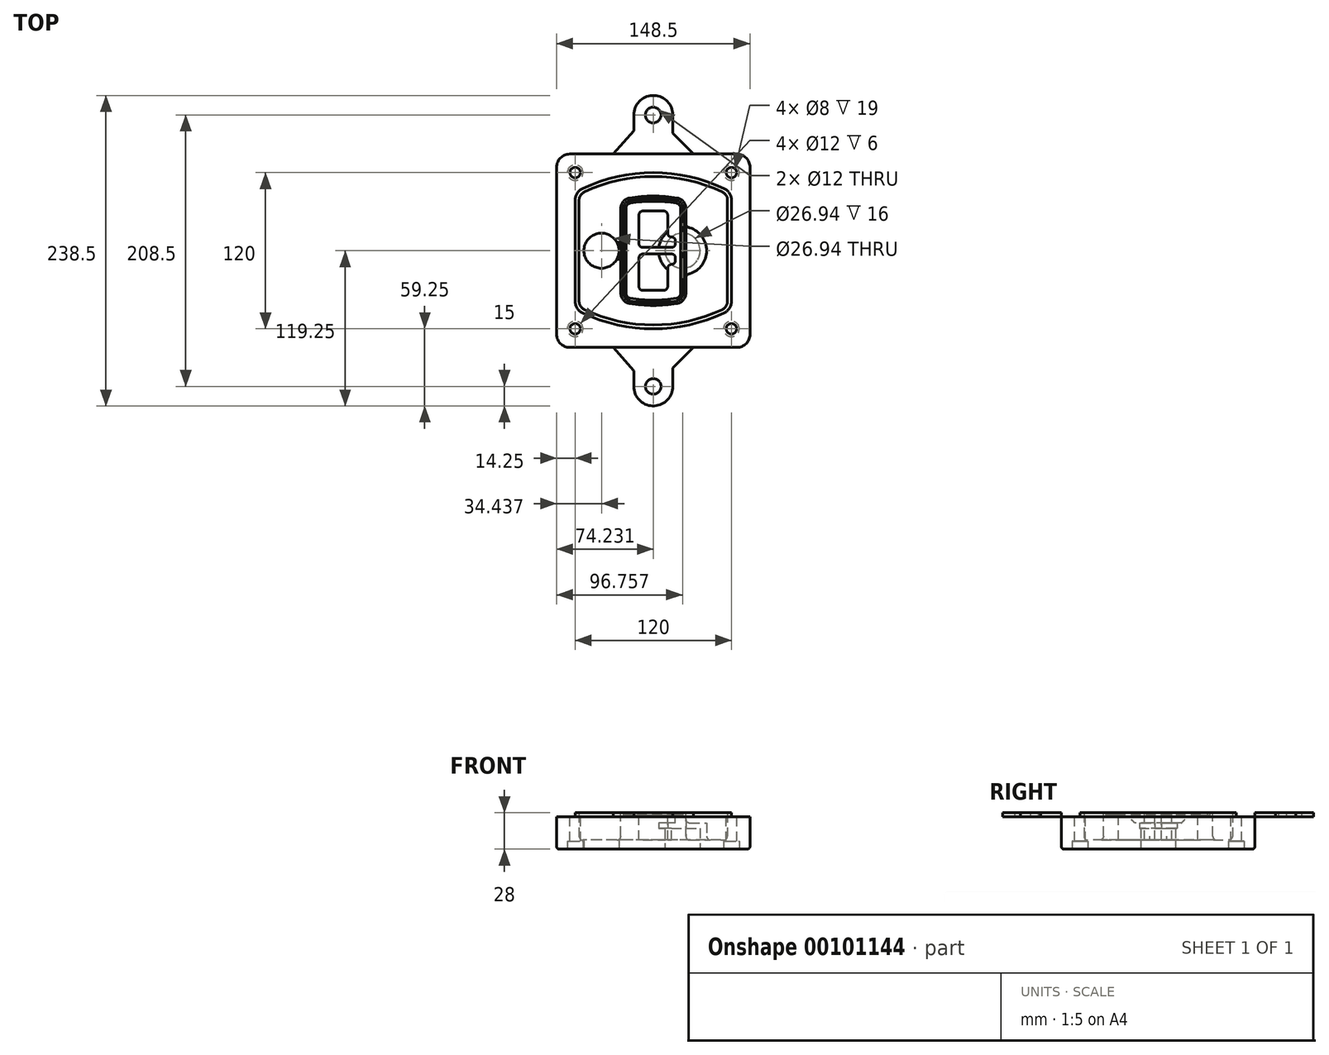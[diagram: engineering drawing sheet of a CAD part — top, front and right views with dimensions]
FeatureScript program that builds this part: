
annotation { "Feature Type Name" : "Feature", "Feature Type Description" : "" }
export const myFeature = defineFeature(function(context is Context, id is Id, definition is map)
    precondition{}
    {
        {
            var Q0;
            Q0=qCreatedBy(makeId("Top.planeOp"),FACE);
            var sketch = newSketch(context, id + "F0", { "sketchPlane" : qUnion([Q0])});
            skPoint(sketch, "E0.rect.middle", {"position": v(0, 0) * mm});
            skLineSegment(sketch, "E1.bottom", {"start": v(-64.25, -74.25) * mm, "end": v(64.25, -74.25) * mm});
            skLineSegment(sketch, "E1.top", {"start": v(-64.25, 74.25) * mm, "end": v(64.25, 74.25) * mm});
            skLineSegment(sketch, "E1.left", {"start": v(-74.25, -64.25) * mm, "end": v(-74.25, 64.25) * mm});
            skLineSegment(sketch, "E1.right", {"start": v(74.25, -64.25) * mm, "end": v(74.25, 64.25) * mm});
            skLineSegment(sketch, "E2", {"start": v(-74.25, 74.25) * mm, "end": v(74.25, -74.25) * mm, "construction": true});
            skLineSegment(sketch, "E3", {"start": v(74.25, 74.25) * mm, "end": v(-74.25, -74.25) * mm, "construction": true});
            skCircle(sketch, "E4", {"center": v(-60, 60) * mm, "radius": 4 * mm});
            skCircle(sketch, "E5", {"center": v(60, 60) * mm, "radius": 4 * mm});
            skCircle(sketch, "E6", {"center": v(60, -60) * mm, "radius": 4 * mm});
            skCircle(sketch, "E7", {"center": v(-60, -60) * mm, "radius": 4 * mm});
            skLineSegment(sketch, "E8", {"start": v(-60, 60) * mm, "end": v(60, 60) * mm, "construction": true});
            skLineSegment(sketch, "E9", {"start": v(60, 60) * mm, "end": v(60, -60) * mm, "construction": true});
            skLineSegment(sketch, "E10", {"start": v(60, -60) * mm, "end": v(-60, -60) * mm, "construction": true});
            skLineSegment(sketch, "E11", {"start": v(-60, -60) * mm, "end": v(-60, 60) * mm, "construction": true});
            skLineSegment(sketch, "E12", {"start": v(-60, 38.83) * mm, "end": v(-60, -38.83) * mm});
            skLineSegment(sketch, "E13", {"start": v(60, 38.83) * mm, "end": v(60, -38.83) * mm});
            skArc(sketch, "E14", {"start": v(54.26, 47.88) * mm, "mid": v(0, 60) * mm, "end": v(-54.26, 47.88) * mm});
            skArc(sketch, "E15", {"start": v(-54.26, -47.88) * mm, "mid": v(0, -60) * mm, "end": v(54.26, -47.88) * mm});
            skLineSegment(sketch, "E16", {"start": v(-60, 0) * mm, "end": v(60, 0) * mm, "construction": true});
            skPoint(sketch, "E17.visualSharp", {"position": v(-60, -45) * mm});
            skArc(sketch, "E17.filletArc", {"start": v(-60, -38.83) * mm, "mid": v(-58.44, -44.2) * mm, "end": v(-54.26, -47.88) * mm});
            skPoint(sketch, "E18.visualSharp", {"position": v(-60, 45) * mm});
            skArc(sketch, "E18.filletArc", {"start": v(-54.26, 47.88) * mm, "mid": v(-58.44, 44.2) * mm, "end": v(-60, 38.83) * mm});
            skPoint(sketch, "E19.visualSharp", {"position": v(60, 45) * mm});
            skArc(sketch, "E19.filletArc", {"start": v(60, 38.83) * mm, "mid": v(58.44, 44.2) * mm, "end": v(54.26, 47.88) * mm});
            skPoint(sketch, "E20.visualSharp", {"position": v(60, -45) * mm});
            skArc(sketch, "E20.filletArc", {"start": v(54.26, -47.88) * mm, "mid": v(58.44, -44.2) * mm, "end": v(60, -38.83) * mm});
            skPoint(sketch, "E21.visualSharp", {"position": v(-74.25, 74.25) * mm});
            skArc(sketch, "E21.filletArc", {"start": v(-64.25, 74.25) * mm, "mid": v(-71.32, 71.32) * mm, "end": v(-74.25, 64.25) * mm});
            skPoint(sketch, "E22.visualSharp", {"position": v(74.25, 74.25) * mm});
            skArc(sketch, "E22.filletArc", {"start": v(74.25, 64.25) * mm, "mid": v(71.32, 71.32) * mm, "end": v(64.25, 74.25) * mm});
            skPoint(sketch, "E23.visualSharp", {"position": v(74.25, -74.25) * mm});
            skArc(sketch, "E23.filletArc", {"start": v(64.25, -74.25) * mm, "mid": v(71.32, -71.32) * mm, "end": v(74.25, -64.25) * mm});
            skPoint(sketch, "E24.visualSharp", {"position": v(-74.25, -74.25) * mm});
            skArc(sketch, "E24.filletArc", {"start": v(-74.25, -64.25) * mm, "mid": v(-71.32, -71.32) * mm, "end": v(-64.25, -74.25) * mm});
            skArc(sketch, "E25.0", {"start": v(57, 38.83) * mm, "mid": v(55.9, 42.58) * mm, "end": v(52.98, 45.17) * mm});
            skLineSegment(sketch, "E25.1", {"start": v(57, 38.83) * mm, "end": v(57, -38.83) * mm});
            skArc(sketch, "E25.2", {"start": v(52.98, -45.17) * mm, "mid": v(55.9, -42.58) * mm, "end": v(57, -38.83) * mm});
            skArc(sketch, "E25.3", {"start": v(-52.98, -45.17) * mm, "mid": v(0, -57) * mm, "end": v(52.98, -45.17) * mm});
            skArc(sketch, "E25.4", {"start": v(-57, -38.83) * mm, "mid": v(-55.9, -42.58) * mm, "end": v(-52.98, -45.17) * mm});
            skArc(sketch, "E25.5", {"start": v(52.98, 45.17) * mm, "mid": v(0, 57) * mm, "end": v(-52.98, 45.17) * mm});
            skLineSegment(sketch, "E25.6", {"start": v(-57, 38.83) * mm, "end": v(-57, -38.83) * mm});
            skArc(sketch, "E25.7", {"start": v(-52.98, 45.17) * mm, "mid": v(-55.9, 42.58) * mm, "end": v(-57, 38.83) * mm});
            skArc(sketch, "E26.0", {"start": v(-55.96, 51.5) * mm, "mid": v(-61.82, 46.33) * mm, "end": v(-64, 38.83) * mm});
            skArc(sketch, "E26.1", {"start": v(55.96, 51.5) * mm, "mid": v(0, 64) * mm, "end": v(-55.96, 51.5) * mm});
            skArc(sketch, "E26.2", {"start": v(64, 38.83) * mm, "mid": v(61.82, 46.33) * mm, "end": v(55.96, 51.5) * mm});
            skLineSegment(sketch, "E26.3", {"start": v(64, 38.83) * mm, "end": v(64, -38.83) * mm});
            skArc(sketch, "E26.4", {"start": v(55.96, -51.5) * mm, "mid": v(61.82, -46.33) * mm, "end": v(64, -38.83) * mm});
            skLineSegment(sketch, "E26.5", {"start": v(-64, 38.83) * mm, "end": v(-64, -38.83) * mm});
            skArc(sketch, "E26.6", {"start": v(-55.96, -51.5) * mm, "mid": v(0, -64) * mm, "end": v(55.96, -51.5) * mm});
            skArc(sketch, "E26.7", {"start": v(-64, -38.83) * mm, "mid": v(-61.82, -46.33) * mm, "end": v(-55.96, -51.5) * mm});
            skSolve(sketch);
        }
        {
            var Q0;
            Q0=makeQuery(id+"F0.imprint","IMPRINT",FACE,{"disambiguationData":[TD([[makeQuery(id+"F0.imprint","IMPRINT",EDGE,{"derivedFrom":sQuery(id+"F0.wireOp",EDGE,"E1.bottom")}),1.0]])]});
            var Q1;
            Q1=makeQuery(id+"F0.imprint","IMPRINT",FACE,{"disambiguationData":[TD([[makeQuery(id+"F0.imprint","IMPRINT",EDGE,{"derivedFrom":sQuery(id+"F0.wireOp",EDGE,"E12")}),1.0]])]});
            var Q2;
            Q2=makeQuery(id+"F0.imprint","IMPRINT",FACE,{"disambiguationData":[TD([[makeQuery(id+"F0.imprint","IMPRINT",EDGE,{"derivedFrom":sQuery(id+"F0.wireOp",EDGE,"E25.0")}),1.0]])]});
            var Q3;
            Q3=makeQuery(id+"F0.imprint","IMPRINT",FACE,{"disambiguationData":[TD([[makeQuery(id+"F0.imprint","IMPRINT",EDGE,{"derivedFrom":sQuery(id+"F0.wireOp",EDGE,"E12")}),-1.0]])]});
            extrude(context, id + "F1", {"entities" : qUnion([Q0, Q1, Q2, Q3]), "oppositeDirection" : true, "depth" : 25 * mm});
        }
        {
            var Q0;
            Q0=makeQuery(id+"F0.imprint","IMPRINT",FACE,{"disambiguationData":[TD([[makeQuery(id+"F0.imprint","IMPRINT",EDGE,{"derivedFrom":sQuery(id+"F0.wireOp",EDGE,"E12")}),1.0]])]});
            extrude(context, id + "F2", {"entities" : qUnion([Q0]), "operationType" : NewBodyOperationType.ADD, "depth" : 3 * mm});
        }
        {
            var Q0;
            Q0=makeQuery(id+"F0.imprint","IMPRINT",FACE,{"disambiguationData":[TD([[makeQuery(id+"F0.imprint","IMPRINT",EDGE,{"derivedFrom":sQuery(id+"F0.wireOp",EDGE,"E25.0")}),1.0]])]});
            extrude(context, id + "F3", {"entities" : qUnion([Q0]), "operationType" : NewBodyOperationType.REMOVE, "oppositeDirection" : true, "depth" : 18 * mm});
        }
        {
            var Q0;
            Q0=makeQuery(id+"F2.opExtrude","CAP_FACE",FACE,{"disambiguationData":[OSD([sQuery(id+"F0.wireOp",EDGE,"E12"),sQuery(id+"F0.wireOp",EDGE,"E13"),sQuery(id+"F0.wireOp",EDGE,"E14"),sQuery(id+"F0.wireOp",EDGE,"E15"),sQuery(id+"F0.wireOp",EDGE,"E17.filletArc"),sQuery(id+"F0.wireOp",EDGE,"E18.filletArc"),sQuery(id+"F0.wireOp",EDGE,"E19.filletArc"),sQuery(id+"F0.wireOp",EDGE,"E20.filletArc"),sQuery(id+"F0.wireOp",EDGE,"E25.0"),sQuery(id+"F0.wireOp",EDGE,"E25.1"),sQuery(id+"F0.wireOp",EDGE,"E25.2"),sQuery(id+"F0.wireOp",EDGE,"E25.3"),sQuery(id+"F0.wireOp",EDGE,"E25.4"),sQuery(id+"F0.wireOp",EDGE,"E25.5"),sQuery(id+"F0.wireOp",EDGE,"E25.6"),sQuery(id+"F0.wireOp",EDGE,"E25.7")])],"isStart":false});
            var sketch = newSketch(context, id + "F4", { "sketchPlane" : qUnion([Q0])});
            skArc(sketch, "E27.0", {"start": v(-18.34, -40.45) * mm, "mid": v(0, -42) * mm, "end": v(18.34, -40.45) * mm});
            skArc(sketch, "E28.0", {"start": v(18.34, 40.45) * mm, "mid": v(0, 42) * mm, "end": v(-18.34, 40.45) * mm});
            skLineSegment(sketch, "E29", {"start": v(-25, 32.57) * mm, "end": v(-25, -32.57) * mm});
            skLineSegment(sketch, "E30", {"start": v(25, 32.57) * mm, "end": v(25, -32.57) * mm});
            skLineSegment(sketch, "E31", {"start": v(-25, 39.1) * mm, "end": v(25, 39.1) * mm, "construction": true});
            skLineSegment(sketch, "E32", {"start": v(-25, -39.1) * mm, "end": v(25, -39.1) * mm, "construction": true});
            skPoint(sketch, "E33.visualSharp", {"position": v(-25, 39.1) * mm});
            skArc(sketch, "E33.filletArc", {"start": v(-18.34, 40.45) * mm, "mid": v(-23.11, 37.73) * mm, "end": v(-25, 32.57) * mm});
            skPoint(sketch, "E34.visualSharp", {"position": v(25, 39.1) * mm});
            skArc(sketch, "E34.filletArc", {"start": v(25, 32.57) * mm, "mid": v(23.11, 37.73) * mm, "end": v(18.34, 40.45) * mm});
            skPoint(sketch, "E35.visualSharp", {"position": v(25, -39.1) * mm});
            skArc(sketch, "E35.filletArc", {"start": v(18.34, -40.45) * mm, "mid": v(23.11, -37.73) * mm, "end": v(25, -32.57) * mm});
            skPoint(sketch, "E36.visualSharp", {"position": v(-25, -39.1) * mm});
            skArc(sketch, "E36.filletArc", {"start": v(-25, -32.57) * mm, "mid": v(-23.11, -37.73) * mm, "end": v(-18.34, -40.45) * mm});
            skArc(sketch, "E37.0", {"start": v(52.98, 45.17) * mm, "mid": v(0, 57) * mm, "end": v(-52.98, 45.17) * mm});
            skArc(sketch, "E37.1", {"start": v(-52.98, 45.17) * mm, "mid": v(-55.9, 42.58) * mm, "end": v(-57, 38.83) * mm});
            skLineSegment(sketch, "E37.2", {"start": v(-57, 38.83) * mm, "end": v(-57, -38.83) * mm});
            skArc(sketch, "E37.3", {"start": v(-57, -38.83) * mm, "mid": v(-55.9, -42.58) * mm, "end": v(-52.98, -45.17) * mm});
            skArc(sketch, "E37.4", {"start": v(-52.98, -45.17) * mm, "mid": v(0, -57) * mm, "end": v(52.98, -45.17) * mm});
            skArc(sketch, "E37.5", {"start": v(52.98, -45.17) * mm, "mid": v(55.9, -42.58) * mm, "end": v(57, -38.83) * mm});
            skLineSegment(sketch, "E37.6", {"start": v(57, 38.83) * mm, "end": v(57, -38.83) * mm});
            skArc(sketch, "E37.7", {"start": v(57, 38.83) * mm, "mid": v(55.9, 42.58) * mm, "end": v(52.98, 45.17) * mm});
            skLineSegment(sketch, "E38.0", {"start": v(23, 32.57) * mm, "end": v(23, -32.57) * mm});
            skArc(sketch, "E38.1", {"start": v(18, -38.48) * mm, "mid": v(21.58, -36.44) * mm, "end": v(23, -32.57) * mm});
            skArc(sketch, "E38.2", {"start": v(-18, -38.48) * mm, "mid": v(0, -40) * mm, "end": v(18, -38.48) * mm});
            skArc(sketch, "E38.3", {"start": v(-23, -32.57) * mm, "mid": v(-21.58, -36.44) * mm, "end": v(-18, -38.48) * mm});
            skLineSegment(sketch, "E38.4", {"start": v(-23, 32.57) * mm, "end": v(-23, -32.57) * mm});
            skArc(sketch, "E38.5", {"start": v(23, 32.57) * mm, "mid": v(21.58, 36.44) * mm, "end": v(18, 38.48) * mm});
            skArc(sketch, "E38.6", {"start": v(-18, 38.48) * mm, "mid": v(-21.58, 36.44) * mm, "end": v(-23, 32.57) * mm});
            skArc(sketch, "E38.7", {"start": v(18, 38.48) * mm, "mid": v(0, 40) * mm, "end": v(-18, 38.48) * mm});
            skArc(sketch, "E39.0", {"start": v(21, 32.57) * mm, "mid": v(20.06, 35.15) * mm, "end": v(17.67, 36.5) * mm});
            skLineSegment(sketch, "E39.1", {"start": v(21, 32.57) * mm, "end": v(21, -32.57) * mm});
            skArc(sketch, "E39.2", {"start": v(17.67, -36.5) * mm, "mid": v(20.06, -35.15) * mm, "end": v(21, -32.57) * mm});
            skArc(sketch, "E39.3", {"start": v(-17.67, -36.5) * mm, "mid": v(0, -38) * mm, "end": v(17.67, -36.5) * mm});
            skArc(sketch, "E39.4", {"start": v(-21, -32.57) * mm, "mid": v(-20.06, -35.15) * mm, "end": v(-17.67, -36.5) * mm});
            skArc(sketch, "E39.5", {"start": v(17.67, 36.5) * mm, "mid": v(0, 38) * mm, "end": v(-17.67, 36.5) * mm});
            skLineSegment(sketch, "E39.6", {"start": v(-21, 32.57) * mm, "end": v(-21, -32.57) * mm});
            skArc(sketch, "E39.7", {"start": v(-17.67, 36.5) * mm, "mid": v(-20.06, 35.15) * mm, "end": v(-21, 32.57) * mm});
            skLineSegment(sketch, "E40", {"start": v(-25, 0) * mm, "end": v(25, 0) * mm, "construction": true});
            skLineSegment(sketch, "E41", {"start": v(-11, 5.5) * mm, "end": v(-11, 27.5) * mm});
            skLineSegment(sketch, "E42", {"start": v(-8, 30.5) * mm, "end": v(8, 30.5) * mm});
            skLineSegment(sketch, "E43", {"start": v(11, 27.5) * mm, "end": v(11, 13.5) * mm});
            skLineSegment(sketch, "E44", {"start": v(14, 10.5) * mm, "end": v(14, 10.5) * mm});
            skLineSegment(sketch, "E45", {"start": v(17, 7.5) * mm, "end": v(17, 5.5) * mm});
            skLineSegment(sketch, "E46", {"start": v(14, 2.5) * mm, "end": v(-8, 2.5) * mm});
            skPoint(sketch, "E47.visualSharp", {"position": v(-11, 30.5) * mm});
            skArc(sketch, "E47.filletArc", {"start": v(-8, 30.5) * mm, "mid": v(-10.12, 29.62) * mm, "end": v(-11, 27.5) * mm});
            skPoint(sketch, "E48.visualSharp", {"position": v(11, 30.5) * mm});
            skArc(sketch, "E48.filletArc", {"start": v(11, 27.5) * mm, "mid": v(10.12, 29.62) * mm, "end": v(8, 30.5) * mm});
            skPoint(sketch, "E49.visualSharp", {"position": v(11, 10.5) * mm});
            skArc(sketch, "E49.filletArc", {"start": v(11, 13.5) * mm, "mid": v(11.88, 11.38) * mm, "end": v(14, 10.5) * mm});
            skPoint(sketch, "E50.visualSharp", {"position": v(17, 10.5) * mm});
            skArc(sketch, "E50.filletArc", {"start": v(17, 7.5) * mm, "mid": v(16.12, 9.62) * mm, "end": v(14, 10.5) * mm});
            skPoint(sketch, "E51.visualSharp", {"position": v(17, 2.5) * mm});
            skArc(sketch, "E51.filletArc", {"start": v(14, 2.5) * mm, "mid": v(16.12, 3.38) * mm, "end": v(17, 5.5) * mm});
            skPoint(sketch, "E52.visualSharp", {"position": v(-11, 2.5) * mm});
            skArc(sketch, "E52.filletArc", {"start": v(-11, 5.5) * mm, "mid": v(-10.12, 3.38) * mm, "end": v(-8, 2.5) * mm});
            skLineSegment(sketch, "E53.0.MirrorCS", {"start": v(14, -2.5) * mm, "end": v(-8, -2.5) * mm});
            skArc(sketch, "E54.0.MirrorCS", {"start": v(-11, -5.5) * mm, "mid": v(-10.12, -3.38) * mm, "end": v(-8, -2.5) * mm});
            skLineSegment(sketch, "E55.0.MirrorCS", {"start": v(-11, -5.5) * mm, "end": v(-11, -27.5) * mm});
            skArc(sketch, "E56.0.MirrorCS", {"start": v(-8, -30.5) * mm, "mid": v(-10.12, -29.62) * mm, "end": v(-11, -27.5) * mm});
            skLineSegment(sketch, "E57.0.MirrorCS", {"start": v(-8, -30.5) * mm, "end": v(8, -30.5) * mm});
            skArc(sketch, "E58.0.MirrorCS", {"start": v(11, -27.5) * mm, "mid": v(10.12, -29.62) * mm, "end": v(8, -30.5) * mm});
            skLineSegment(sketch, "E59.0.MirrorCS", {"start": v(11, -27.5) * mm, "end": v(11, -13.5) * mm});
            skArc(sketch, "E60.0.MirrorCS", {"start": v(11, -13.5) * mm, "mid": v(11.88, -11.38) * mm, "end": v(14, -10.5) * mm});
            skArc(sketch, "E61.0.MirrorCS", {"start": v(17, -7.5) * mm, "mid": v(16.12, -9.62) * mm, "end": v(14, -10.5) * mm});
            skLineSegment(sketch, "E62.0.MirrorCS", {"start": v(17, -7.5) * mm, "end": v(17, -5.5) * mm});
            skArc(sketch, "E63.0.MirrorCS", {"start": v(14, -2.5) * mm, "mid": v(16.12, -3.38) * mm, "end": v(17, -5.5) * mm});
            skSolve(sketch);
        }
        {
            var Q0;
            Q0=makeQuery(id+"F4.imprint","IMPRINT",FACE,{"disambiguationData":[TD([[makeQuery(id+"F4.imprint","IMPRINT",EDGE,{"derivedFrom":sQuery(id+"F4.wireOp",EDGE,"E27.0")}),1.0]])]});
            var Q1;
            Q1=makeQuery(id+"F4.imprint","IMPRINT",FACE,{"disambiguationData":[TD([[makeQuery(id+"F4.imprint","IMPRINT",EDGE,{"derivedFrom":sQuery(id+"F4.wireOp",EDGE,"E38.0")}),-1.0]])]});
            var Q2;
            Q2=makeQuery(id+"F4.imprint","IMPRINT",FACE,{"disambiguationData":[TD([[makeQuery(id+"F4.imprint","IMPRINT",EDGE,{"derivedFrom":sQuery(id+"F4.wireOp",EDGE,"E39.0")}),1.0]])]});
            extrude(context, id + "F5", {"entities" : qUnion([Q0, Q1, Q2]), "operationType" : NewBodyOperationType.ADD, "endBound" : BoundingType.UP_TO_NEXT, "oppositeDirection" : true, "depth" : 25 * mm});
        }
        {
            var Q0;
            Q0=makeQuery(id+"F4.imprint","IMPRINT",FACE,{"disambiguationData":[TD([[makeQuery(id+"F4.imprint","IMPRINT",EDGE,{"derivedFrom":sQuery(id+"F4.wireOp",EDGE,"E38.0")}),-1.0]])]});
            extrude(context, id + "F6", {"entities" : qUnion([Q0]), "operationType" : NewBodyOperationType.REMOVE, "oppositeDirection" : true, "depth" : 2 * mm});
        }
        {
            var Q0;
            Q0=makeQuery(id+"F1.opExtrude","CAP_FACE",FACE,{"disambiguationData":[OSD([sQuery(id+"F0.wireOp",EDGE,"E1.bottom"),sQuery(id+"F0.wireOp",EDGE,"E1.top"),sQuery(id+"F0.wireOp",EDGE,"E1.left"),sQuery(id+"F0.wireOp",EDGE,"E1.right"),sQuery(id+"F0.wireOp",EDGE,"E4"),sQuery(id+"F0.wireOp",EDGE,"E5"),sQuery(id+"F0.wireOp",EDGE,"E6"),sQuery(id+"F0.wireOp",EDGE,"E7"),sQuery(id+"F0.wireOp",EDGE,"E21.filletArc"),sQuery(id+"F0.wireOp",EDGE,"E22.filletArc"),sQuery(id+"F0.wireOp",EDGE,"E23.filletArc"),sQuery(id+"F0.wireOp",EDGE,"E24.filletArc")])],"isStart":false});
            var sketch = newSketch(context, id + "F7", { "sketchPlane" : qUnion([Q0])});
            skCircle(sketch, "E64", {"center": v(22.5, 0) * mm, "radius": 13.47 * mm});
            skCircle(sketch, "E65", {"center": v(-39.81, 0) * mm, "radius": 13.47 * mm});
            skLineSegment(sketch, "E66", {"start": v(74.25, 0) * mm, "end": v(-74.25, 0) * mm});
            skCircle(sketch, "E67", {"center": v(22.5, 0) * mm, "radius": 18.47 * mm});
            skCircle(sketch, "E68", {"center": v(60, -60) * mm, "radius": 6 * mm});
            skCircle(sketch, "E69", {"center": v(-60, -60) * mm, "radius": 6 * mm});
            skCircle(sketch, "E70", {"center": v(-60, 60) * mm, "radius": 6 * mm});
            skCircle(sketch, "E71", {"center": v(60, 60) * mm, "radius": 6 * mm});
            skSolve(sketch);
        }
        {
            var Q0;
            {var subQ1=sQuery(id+"F7.wireOp",EDGE,"E66");var subQ4=sQuery(id+"F7.wireOp",EDGE,"E64");var subQ6=makeQuery(id+"F7.imprint","INTERSECT",VERTEX,{"disambiguationData":[OD(0.0)],"derivedFrom":[subQ4,subQ1]});Q0=makeQuery(id+"F7.imprint","IMPRINT",FACE,{"disambiguationData":[TD([[makeQuery(id+"F7.imprint","IMPRINT",EDGE,{"disambiguationData":[TD([[subQ6,-1.0]])],"derivedFrom":subQ4}),-1.0]])]});}
            var Q1;
            {var subQ0=sQuery(id+"F7.wireOp",EDGE,"E66");var subQ1=sQuery(id+"F7.wireOp",EDGE,"E64");var subQ3=makeQuery(id+"F7.imprint","INTERSECT",VERTEX,{"disambiguationData":[OD(0.0)],"derivedFrom":[subQ1,subQ0]});Q1=makeQuery(id+"F7.imprint","IMPRINT",FACE,{"disambiguationData":[TD([[makeQuery(id+"F7.imprint","IMPRINT",EDGE,{"disambiguationData":[TD([[subQ3,-1.0]])],"derivedFrom":subQ1}),1.0]])]});}
            var Q2;
            {var subQ0=sQuery(id+"F7.wireOp",EDGE,"E66");var subQ1=sQuery(id+"F7.wireOp",EDGE,"E64");var subQ3=makeQuery(id+"F7.imprint","INTERSECT",VERTEX,{"disambiguationData":[OD(0.0)],"derivedFrom":[subQ1,subQ0]});Q2=makeQuery(id+"F7.imprint","IMPRINT",FACE,{"disambiguationData":[TD([[makeQuery(id+"F7.imprint","IMPRINT",EDGE,{"disambiguationData":[TD([[subQ3,1.0]])],"derivedFrom":subQ1}),1.0]])]});}
            var Q3;
            {var subQ1=sQuery(id+"F7.wireOp",EDGE,"E66");var subQ4=sQuery(id+"F7.wireOp",EDGE,"E64");var subQ6=makeQuery(id+"F7.imprint","INTERSECT",VERTEX,{"disambiguationData":[OD(0.0)],"derivedFrom":[subQ4,subQ1]});Q3=makeQuery(id+"F7.imprint","IMPRINT",FACE,{"disambiguationData":[TD([[makeQuery(id+"F7.imprint","IMPRINT",EDGE,{"disambiguationData":[TD([[subQ6,1.0]])],"derivedFrom":subQ4}),-1.0]])]});}
            extrude(context, id + "F8", {"entities" : qUnion([Q0, Q1, Q2, Q3]), "operationType" : NewBodyOperationType.ADD, "oppositeDirection" : true, "depth" : 20 * mm});
        }
        {
            var Q0;
            {var subQ0=sQuery(id+"F7.wireOp",EDGE,"E66");var subQ1=sQuery(id+"F7.wireOp",EDGE,"E64");var subQ3=makeQuery(id+"F7.imprint","INTERSECT",VERTEX,{"disambiguationData":[OD(0.0)],"derivedFrom":[subQ1,subQ0]});Q0=makeQuery(id+"F7.imprint","IMPRINT",FACE,{"disambiguationData":[TD([[makeQuery(id+"F7.imprint","IMPRINT",EDGE,{"disambiguationData":[TD([[subQ3,-1.0]])],"derivedFrom":subQ1}),1.0]])]});}
            var Q1;
            {var subQ0=sQuery(id+"F7.wireOp",EDGE,"E66");var subQ1=sQuery(id+"F7.wireOp",EDGE,"E64");var subQ3=makeQuery(id+"F7.imprint","INTERSECT",VERTEX,{"disambiguationData":[OD(0.0)],"derivedFrom":[subQ1,subQ0]});Q1=makeQuery(id+"F7.imprint","IMPRINT",FACE,{"disambiguationData":[TD([[makeQuery(id+"F7.imprint","IMPRINT",EDGE,{"disambiguationData":[TD([[subQ3,1.0]])],"derivedFrom":subQ1}),1.0]])]});}
            extrude(context, id + "F9", {"entities" : qUnion([Q0, Q1]), "operationType" : NewBodyOperationType.REMOVE, "oppositeDirection" : true, "depth" : 16 * mm});
        }
        {
            var Q0;
            {var subQ0=sQuery(id+"F7.wireOp",EDGE,"E66");var subQ1=sQuery(id+"F7.wireOp",EDGE,"E65");var subQ3=makeQuery(id+"F7.imprint","INTERSECT",VERTEX,{"disambiguationData":[OD(0.0)],"derivedFrom":[subQ1,subQ0]});Q0=makeQuery(id+"F7.imprint","IMPRINT",FACE,{"disambiguationData":[TD([[makeQuery(id+"F7.imprint","IMPRINT",EDGE,{"disambiguationData":[TD([[subQ3,-1.0]])],"derivedFrom":subQ1}),1.0]])]});}
            var Q1;
            {var subQ0=sQuery(id+"F7.wireOp",EDGE,"E66");var subQ1=sQuery(id+"F7.wireOp",EDGE,"E65");var subQ3=makeQuery(id+"F7.imprint","INTERSECT",VERTEX,{"disambiguationData":[OD(0.0)],"derivedFrom":[subQ1,subQ0]});Q1=makeQuery(id+"F7.imprint","IMPRINT",FACE,{"disambiguationData":[TD([[makeQuery(id+"F7.imprint","IMPRINT",EDGE,{"disambiguationData":[TD([[subQ3,1.0]])],"derivedFrom":subQ1}),1.0]])]});}
            extrude(context, id + "F10", {"entities" : qUnion([Q0, Q1]), "operationType" : NewBodyOperationType.REMOVE, "oppositeDirection" : true, "depth" : 25 * mm});
        }
        {
            var Q0;
            Q0=makeQuery(id+"F7.imprint","IMPRINT",FACE,{"disambiguationData":[TD([[makeQuery(id+"F7.imprint","IMPRINT",EDGE,{"derivedFrom":sQuery(id+"F7.wireOp",EDGE,"E68")}),1.0]])]});
            var Q1;
            Q1=makeQuery(id+"F7.imprint","IMPRINT",FACE,{"disambiguationData":[TD([[makeQuery(id+"F7.imprint","IMPRINT",EDGE,{"derivedFrom":makeQuery(id+"F1.opExtrude","CAP_EDGE",EDGE,{"disambiguationData":[OSD([sQuery(id+"F0.wireOp",EDGE,"E5")])],"isStart":false})}),-1.0]])]});
            var Q2;
            Q2=makeQuery(id+"F7.imprint","IMPRINT",FACE,{"disambiguationData":[TD([[makeQuery(id+"F7.imprint","IMPRINT",EDGE,{"derivedFrom":sQuery(id+"F7.wireOp",EDGE,"E69")}),1.0]])]});
            var Q3;
            Q3=makeQuery(id+"F7.imprint","IMPRINT",FACE,{"disambiguationData":[TD([[makeQuery(id+"F7.imprint","IMPRINT",EDGE,{"derivedFrom":makeQuery(id+"F1.opExtrude","CAP_EDGE",EDGE,{"disambiguationData":[OSD([sQuery(id+"F0.wireOp",EDGE,"E4")])],"isStart":false})}),-1.0]])]});
            var Q4;
            Q4=makeQuery(id+"F7.imprint","IMPRINT",FACE,{"disambiguationData":[TD([[makeQuery(id+"F7.imprint","IMPRINT",EDGE,{"derivedFrom":sQuery(id+"F7.wireOp",EDGE,"E70")}),1.0]])]});
            var Q5;
            Q5=makeQuery(id+"F7.imprint","IMPRINT",FACE,{"disambiguationData":[TD([[makeQuery(id+"F7.imprint","IMPRINT",EDGE,{"derivedFrom":makeQuery(id+"F1.opExtrude","CAP_EDGE",EDGE,{"disambiguationData":[OSD([sQuery(id+"F0.wireOp",EDGE,"E7")])],"isStart":false})}),-1.0]])]});
            var Q6;
            Q6=makeQuery(id+"F7.imprint","IMPRINT",FACE,{"disambiguationData":[TD([[makeQuery(id+"F7.imprint","IMPRINT",EDGE,{"derivedFrom":sQuery(id+"F7.wireOp",EDGE,"E71")}),1.0]])]});
            var Q7;
            Q7=makeQuery(id+"F7.imprint","IMPRINT",FACE,{"disambiguationData":[TD([[makeQuery(id+"F7.imprint","IMPRINT",EDGE,{"derivedFrom":makeQuery(id+"F1.opExtrude","CAP_EDGE",EDGE,{"disambiguationData":[OSD([sQuery(id+"F0.wireOp",EDGE,"E6")])],"isStart":false})}),-1.0]])]});
            extrude(context, id + "F11", {"entities" : qUnion([Q0, Q1, Q2, Q3, Q4, Q5, Q6, Q7]), "operationType" : NewBodyOperationType.REMOVE, "oppositeDirection" : true, "depth" : 6 * mm});
        }
        {
            var Q0;
            Q0=makeQuery(id+"F9.boolean.opBoolean","COPY",FACE,{"derivedFrom":makeQuery(id+"F9.opExtrude","CAP_FACE",FACE,{"disambiguationData":[OSD([sQuery(id+"F7.wireOp",EDGE,"E64")])],"isStart":false})});
            var sketch = newSketch(context, id + "F12", { "sketchPlane" : qUnion([Q0])});
            skArc(sketch, "E72.0", {"start": v(11, 14.45) * mm, "mid": v(6.45, 9.13) * mm, "end": v(4.2, 2.5) * mm});
            skArc(sketch, "E72.1", {"start": v(4.2, -2.5) * mm, "mid": v(6.45, -9.13) * mm, "end": v(11, -14.45) * mm});
            skLineSegment(sketch, "E73", {"start": v(4.2, -2.5) * mm, "end": v(14, -2.5) * mm});
            skLineSegment(sketch, "E74.0", {"start": v(14, 2.5) * mm, "end": v(4.2, 2.5) * mm});
            skArc(sketch, "E74.1", {"start": v(14, 2.5) * mm, "mid": v(16.12, 3.38) * mm, "end": v(17, 5.5) * mm});
            skLineSegment(sketch, "E74.2", {"start": v(17, 7.5) * mm, "end": v(17, 5.5) * mm});
            skArc(sketch, "E74.3", {"start": v(17, 7.5) * mm, "mid": v(16.12, 9.62) * mm, "end": v(14, 10.5) * mm});
            skArc(sketch, "E74.4", {"start": v(11, 13.5) * mm, "mid": v(11.88, 11.38) * mm, "end": v(14, 10.5) * mm});
            skLineSegment(sketch, "E74.5", {"start": v(11, 14.45) * mm, "end": v(11, 13.5) * mm});
            skLineSegment(sketch, "E74.7", {"start": v(14, -2.5) * mm, "end": v(4.2, -2.5) * mm});
            skArc(sketch, "E74.8", {"start": v(14, -2.5) * mm, "mid": v(16.12, -3.38) * mm, "end": v(17, -5.5) * mm});
            skLineSegment(sketch, "E74.9", {"start": v(17, -7.5) * mm, "end": v(17, -5.5) * mm});
            skArc(sketch, "E74.10", {"start": v(17, -7.5) * mm, "mid": v(16.12, -9.62) * mm, "end": v(14, -10.5) * mm});
            skArc(sketch, "E74.11", {"start": v(11, -13.5) * mm, "mid": v(11.88, -11.38) * mm, "end": v(14, -10.5) * mm});
            skLineSegment(sketch, "E74.12", {"start": v(11, -14.45) * mm, "end": v(11, -13.5) * mm});
            skPoint(sketch, "E75.orphan", {"position": v(11, -27.5) * mm});
            skPoint(sketch, "E76.orphan", {"position": v(-8, -2.5) * mm});
            skPoint(sketch, "E77.orphan", {"position": v(-8, 2.5) * mm});
            skPoint(sketch, "E78.orphan", {"position": v(11, 27.5) * mm});
            skSolve(sketch);
        }
        {
            var Q0;
            {var subQ7=sQuery(id+"F12.wireOp",EDGE,"E72.0");var subQ14=sQuery(id+"F12.wireOp",EDGE,"E72.1");var subQ16=sQuery(id+"F12.wireOp",EDGE,"E74.1");var subQ18=sQuery(id+"F12.wireOp",EDGE,"E74.8");Q0=qUnion([makeQuery(id+"F12.imprint","IMPRINT",FACE,{"disambiguationData":[TD([[makeQuery(id+"F12.imprint","IMPRINT",EDGE,{"derivedFrom":subQ7}),1.0]])]}),makeQuery(id+"F12.imprint","IMPRINT",FACE,{"disambiguationData":[TD([[makeQuery(id+"F12.imprint","IMPRINT",EDGE,{"derivedFrom":subQ14}),1.0]])]}),makeQuery(id+"F12.imprint","IMPRINT",FACE,{"disambiguationData":[TD([[makeQuery(id+"F12.imprint","IMPRINT",EDGE,{"derivedFrom":subQ16}),1.0]])]}),makeQuery(id+"F12.imprint","IMPRINT",FACE,{"disambiguationData":[TD([[makeQuery(id+"F12.imprint","IMPRINT",EDGE,{"derivedFrom":subQ18}),-1.0]])]})]);}
            var Q1;
            Q1=makeQuery(id+"F5.boolean.opBoolean","SPLIT",FACE,{"disambiguationData":[TD([makeQuery(id+"F5.opExtrude","SWEPT_FACE",FACE,{"disambiguationData":[OSD([sQuery(id+"F4.wireOp",EDGE,"E41")])]})])],"derivedFrom":makeQuery(id+"F3.boolean.opBoolean","COPY",FACE,{"derivedFrom":makeQuery(id+"F3.opExtrude","CAP_FACE",FACE,{"disambiguationData":[OSD([sQuery(id+"F0.wireOp",EDGE,"E25.0"),sQuery(id+"F0.wireOp",EDGE,"E25.1"),sQuery(id+"F0.wireOp",EDGE,"E25.2"),sQuery(id+"F0.wireOp",EDGE,"E25.3"),sQuery(id+"F0.wireOp",EDGE,"E25.4"),sQuery(id+"F0.wireOp",EDGE,"E25.5"),sQuery(id+"F0.wireOp",EDGE,"E25.6"),sQuery(id+"F0.wireOp",EDGE,"E25.7")])],"isStart":false})})});
            extrude(context, id + "F13", {"entities" : qUnion([Q0]), "operationType" : NewBodyOperationType.REMOVE, "endBound" : BoundingType.UP_TO_SURFACE, "endBoundEntityFace" : qUnion([Q1]), "depth" : 25 * mm});
        }
        {
            var Q0;
            Q0=makeQuery(id+"F3.boolean.opBoolean","COPY",EDGE,{"derivedFrom":makeQuery(id+"F3.opExtrude","CAP_EDGE",EDGE,{"disambiguationData":[OSD([sQuery(id+"F0.wireOp",EDGE,"E25.6")])],"isStart":false})});
            var Q1;
            Q1=makeQuery(id+"F8.boolean.opBoolean","INTERSECT",EDGE,{"derivedFrom":[makeQuery(id+"F5.opExtrude","SWEPT_FACE",FACE,{"disambiguationData":[OSD([sQuery(id+"F4.wireOp",EDGE,"E30")])]}),makeQuery(id+"F8.opExtrude","CAP_FACE",FACE,{"disambiguationData":[OSD([sQuery(id+"F7.wireOp",EDGE,"E67")])],"isStart":false})]});
            var Q2;
            Q2=makeQuery(id+"F8.boolean.opBoolean","INTERSECT",EDGE,{"disambiguationData":[OD(1.0)],"derivedFrom":[makeQuery(id+"F5.opExtrude","SWEPT_FACE",FACE,{"disambiguationData":[OSD([sQuery(id+"F4.wireOp",EDGE,"E30")])]}),makeQuery(id+"F8.opExtrude","SWEPT_FACE",FACE,{"disambiguationData":[OSD([sQuery(id+"F7.wireOp",EDGE,"E67")])]})]});
            var Q3;
            {var subQ0=sQuery(id+"F4.wireOp",EDGE,"E30");Q3=makeQuery(id+"F8.boolean.opBoolean","SPLIT",EDGE,{"disambiguationData":[TD([makeQuery(id+"F5.opExtrude","SWEPT_FACE",FACE,{"disambiguationData":[OSD([sQuery(id+"F4.wireOp",EDGE,"E35.filletArc")])]})])],"derivedFrom":makeQuery(id+"F5.opExtrude","CAP_EDGE",EDGE,{"disambiguationData":[OSD([subQ0])],"isStart":false})});}
            var Q4;
            {var subQ0=sQuery(id+"F0.wireOp",EDGE,"E25.7");var subQ1=sQuery(id+"F0.wireOp",EDGE,"E25.1");var subQ2=sQuery(id+"F0.wireOp",EDGE,"E25.6");var subQ3=sQuery(id+"F0.wireOp",EDGE,"E25.5");var subQ4=sQuery(id+"F0.wireOp",EDGE,"E25.4");var subQ5=sQuery(id+"F0.wireOp",EDGE,"E25.0");var subQ6=sQuery(id+"F0.wireOp",EDGE,"E25.2");var subQ7=sQuery(id+"F0.wireOp",EDGE,"E25.3");Q4=makeQuery(id+"F8.boolean.opBoolean","INTERSECT",EDGE,{"derivedFrom":[makeQuery(id+"F5.boolean.opBoolean","SPLIT",FACE,{"disambiguationData":[TD([makeQuery(id+"F2.opExtrude","SWEPT_FACE",FACE,{"disambiguationData":[OSD([subQ5])]})])],"derivedFrom":makeQuery(id+"F3.boolean.opBoolean","COPY",FACE,{"derivedFrom":makeQuery(id+"F3.opExtrude","CAP_FACE",FACE,{"disambiguationData":[OSD([subQ5,subQ1,subQ6,subQ7,subQ4,subQ3,subQ2,subQ0])],"isStart":false})})}),makeQuery(id+"F8.opExtrude","SWEPT_FACE",FACE,{"disambiguationData":[OSD([sQuery(id+"F7.wireOp",EDGE,"E67")])]})]});}
            var Q5;
            Q5=makeQuery(id+"F8.boolean.opBoolean","INTERSECT",EDGE,{"disambiguationData":[OD(0.0)],"derivedFrom":[makeQuery(id+"F5.opExtrude","SWEPT_FACE",FACE,{"disambiguationData":[OSD([sQuery(id+"F4.wireOp",EDGE,"E30")])]}),makeQuery(id+"F8.opExtrude","SWEPT_FACE",FACE,{"disambiguationData":[OSD([sQuery(id+"F7.wireOp",EDGE,"E67")])]})]});
            fillet(context, id + "F14", {"entities" : qUnion([Q0, Q1, Q2, Q3, Q4, Q5]), "radius" : 3 * mm, "tangentPropagation" : true, "allowEdgeOverflow" : false});
        }
        {
            var Q0;
            Q0=makeQuery(id+"F1.opExtrude","CAP_EDGE",EDGE,{"disambiguationData":[OSD([sQuery(id+"F0.wireOp",EDGE,"E1.bottom")])],"isStart":false});
            fillet(context, id + "F15", {"entities" : qUnion([Q0]), "radius" : 2 * mm, "tangentPropagation" : true, "allowEdgeOverflow" : false});
        }
        {
            var Q0;
            {var subQ0=sQuery(id+"F0.wireOp",EDGE,"E22.filletArc");var subQ1=sQuery(id+"F0.wireOp",EDGE,"E7");var subQ2=sQuery(id+"F0.wireOp",EDGE,"E6");var subQ3=sQuery(id+"F0.wireOp",EDGE,"E5");var subQ4=sQuery(id+"F0.wireOp",EDGE,"E4");var subQ5=sQuery(id+"F0.wireOp",EDGE,"E1.bottom");var subQ6=sQuery(id+"F0.wireOp",EDGE,"E21.filletArc");var subQ7=sQuery(id+"F0.wireOp",EDGE,"E1.top");var subQ8=sQuery(id+"F0.wireOp",EDGE,"E1.left");var subQ9=sQuery(id+"F0.wireOp",EDGE,"E1.right");var subQ10=sQuery(id+"F0.wireOp",EDGE,"E23.filletArc");var subQ11=sQuery(id+"F0.wireOp",EDGE,"E24.filletArc");Q0=makeQuery(id+"F2.boolean.opBoolean","SPLIT",FACE,{"disambiguationData":[TD([makeQuery(id+"F1.opExtrude","SWEPT_FACE",FACE,{"disambiguationData":[OSD([subQ5])]})])],"derivedFrom":makeQuery(id+"F1.opExtrude","CAP_FACE",FACE,{"disambiguationData":[OSD([subQ5,subQ7,subQ8,subQ9,subQ4,subQ3,subQ2,subQ1,subQ6,subQ0,subQ10,subQ11])],"isStart":true})});}
            var sketch = newSketch(context, id + "F16", { "sketchPlane" : qUnion([Q0])});
            skLineSegment(sketch, "E79", {"start": v(-30.9, 74.25) * mm, "end": v(-15.02, 92.25) * mm});
            skLineSegment(sketch, "E80", {"start": v(-15.02, 92.25) * mm, "end": v(-15.02, 104.25) * mm});
            skLineSegment(sketch, "E81", {"start": v(14.92, 90.13) * mm, "end": v(14.92, 105.6) * mm});
            skArc(sketch, "E82", {"start": v(14.92, 105.6) * mm, "mid": v(-0.69, 119.23) * mm, "end": v(-15.02, 104.25) * mm});
            skCircle(sketch, "E83", {"center": v(-0.02, 104.25) * mm, "radius": 6 * mm});
            skLineSegment(sketch, "E84", {"start": v(-0.02, 104.25) * mm, "end": v(-0.02, 74.25) * mm});
            skLineSegment(sketch, "E85", {"start": v(-74.25, 0) * mm, "end": v(74.25, 0) * mm, "construction": true});
            skLineSegment(sketch, "E86", {"start": v(14.92, 90.13) * mm, "end": v(30.8, 74.25) * mm});
            skLineSegment(sketch, "E87.MirrorCS", {"start": v(14.92, -90.13) * mm, "end": v(30.8, -74.25) * mm});
            skLineSegment(sketch, "E88.MirrorCS", {"start": v(14.92, -90.13) * mm, "end": v(14.92, -105.6) * mm});
            skArc(sketch, "E89.MirrorCS", {"start": v(14.92, -105.6) * mm, "mid": v(-0.69, -119.23) * mm, "end": v(-15.02, -104.25) * mm});
            skLineSegment(sketch, "E90.MirrorCS", {"start": v(-15.02, -92.25) * mm, "end": v(-15.02, -104.25) * mm});
            skLineSegment(sketch, "E91.MirrorCS", {"start": v(-30.9, -74.25) * mm, "end": v(-15.02, -92.25) * mm});
            skLineSegment(sketch, "E92.MirrorCS", {"start": v(-0.02, -104.25) * mm, "end": v(-0.02, -74.25) * mm});
            skCircle(sketch, "E93.MirrorC", {"center": v(-0.02, -104.25) * mm, "radius": 6 * mm});
            skSolve(sketch);
        }
        {
            var Q0;
            {var subQ3=sQuery(id+"F16.wireOp",EDGE,"E87.MirrorCS");Q0=makeQuery(id+"F16.imprint","IMPRINT",FACE,{"disambiguationData":[TD([[makeQuery(id+"F16.imprint","IMPRINT",EDGE,{"derivedFrom":subQ3}),1.0]])]});}
            var Q1;
            {var subQ1=sQuery(id+"F16.wireOp",EDGE,"E79");Q1=makeQuery(id+"F16.imprint","IMPRINT",FACE,{"disambiguationData":[TD([[makeQuery(id+"F16.imprint","IMPRINT",EDGE,{"derivedFrom":subQ1}),-1.0]])]});}
            var Q2;
            Q2=makeQuery(id+"F2.opExtrude","CAP_FACE",FACE,{"disambiguationData":[OSD([sQuery(id+"F0.wireOp",EDGE,"E12"),sQuery(id+"F0.wireOp",EDGE,"E13"),sQuery(id+"F0.wireOp",EDGE,"E14"),sQuery(id+"F0.wireOp",EDGE,"E15"),sQuery(id+"F0.wireOp",EDGE,"E17.filletArc"),sQuery(id+"F0.wireOp",EDGE,"E18.filletArc"),sQuery(id+"F0.wireOp",EDGE,"E19.filletArc"),sQuery(id+"F0.wireOp",EDGE,"E20.filletArc"),sQuery(id+"F0.wireOp",EDGE,"E25.0"),sQuery(id+"F0.wireOp",EDGE,"E25.1"),sQuery(id+"F0.wireOp",EDGE,"E25.2"),sQuery(id+"F0.wireOp",EDGE,"E25.3"),sQuery(id+"F0.wireOp",EDGE,"E25.4"),sQuery(id+"F0.wireOp",EDGE,"E25.5"),sQuery(id+"F0.wireOp",EDGE,"E25.6"),sQuery(id+"F0.wireOp",EDGE,"E25.7")])],"isStart":false});
            extrude(context, id + "F17", {"entities" : qUnion([Q0, Q1]), "endBound" : BoundingType.UP_TO_SURFACE, "endBoundEntityFace" : qUnion([Q2]), "depth" : 25 * mm});
        }
    });
